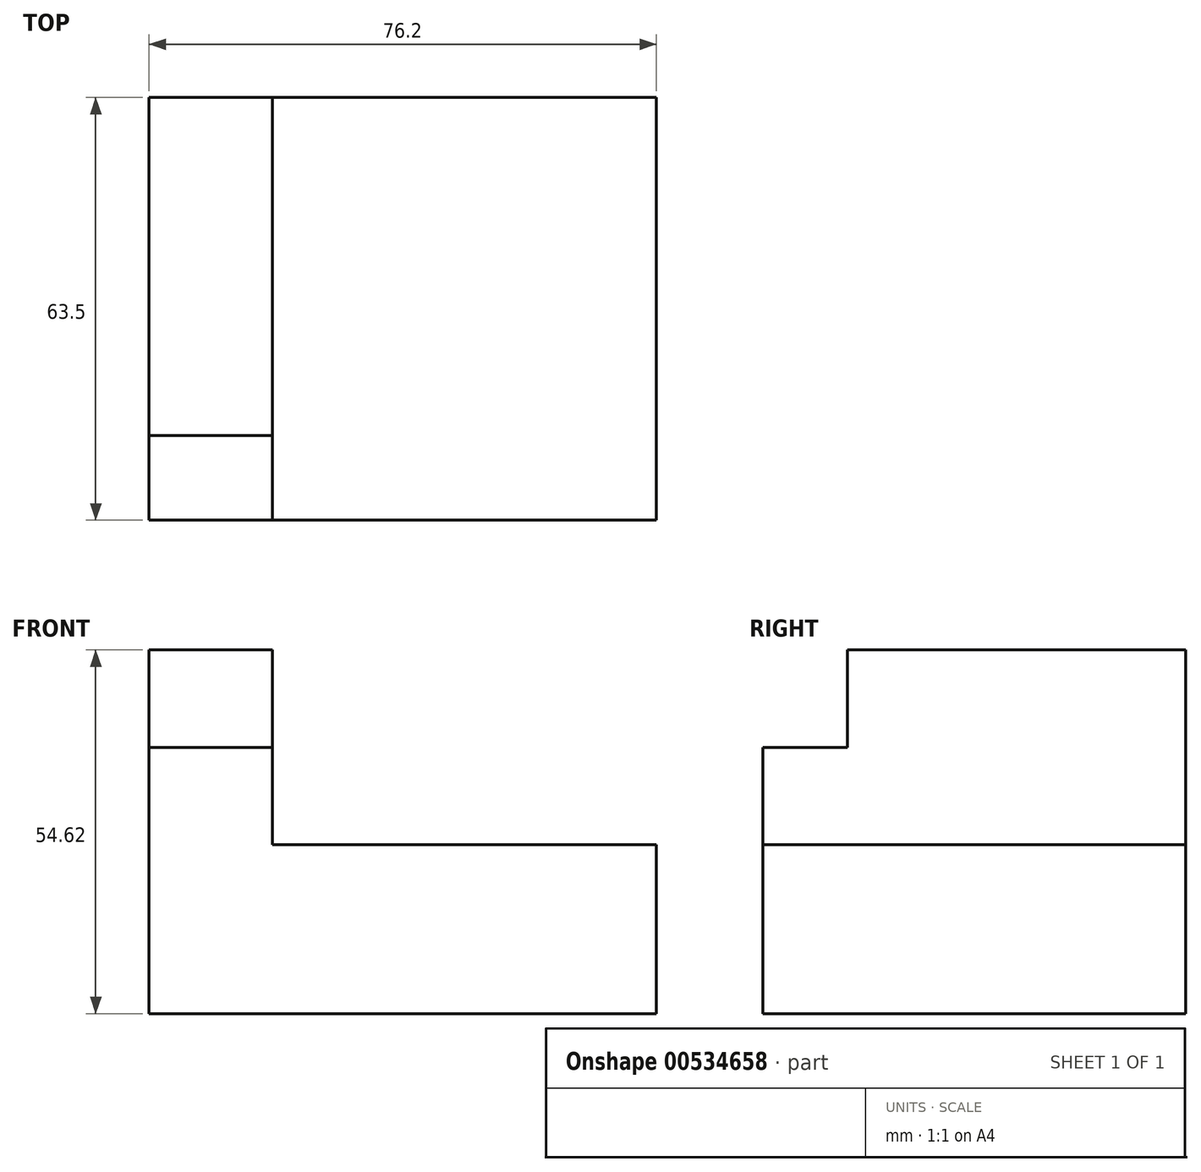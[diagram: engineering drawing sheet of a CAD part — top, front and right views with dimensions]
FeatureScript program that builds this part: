
annotation { "Feature Type Name" : "Feature", "Feature Type Description" : "" }
export const myFeature = defineFeature(function(context is Context, id is Id, definition is map)
    precondition{}
    {
        {
            var Q0;
            Q0=qCreatedBy(makeId("Top.planeOp"),FACE);
            var sketch = newSketch(context, id + "F0", { "sketchPlane" : qUnion([Q0])});
            skLineSegment(sketch, "E0.bottom", {"start": v(-36.12, 34.38) * mm, "end": v(40.08, 34.38) * mm});
            skLineSegment(sketch, "E0.top", {"start": v(-36.12, -29.12) * mm, "end": v(40.08, -29.12) * mm});
            skLineSegment(sketch, "E0.left", {"start": v(-36.12, 34.38) * mm, "end": v(-36.12, -29.12) * mm});
            skLineSegment(sketch, "E0.right", {"start": v(40.08, 34.38) * mm, "end": v(40.08, -29.12) * mm});
            skSolve(sketch);
        }
        {
            var Q0;
            Q0=makeQuery(id+"F0.imprint","IMPRINT",FACE,{"disambiguationData":[TD([[makeQuery(id+"F0.imprint","IMPRINT",EDGE,{"derivedFrom":sQuery(id+"F0.wireOp",EDGE,"E0.bottom")}),-1.0]])]});
            extrude(context, id + "F1", {"entities" : qUnion([Q0]), "depth" : 25.4 * mm, "offsetDistance" : 25.4 * mm});
        }
        {
            var Q0;
            Q0=makeQuery(id+"F1.opExtrude","SWEPT_FACE",FACE,{"disambiguationData":[OSD([sQuery(id+"F0.wireOp",EDGE,"E0.top")])]});
            var sketch = newSketch(context, id + "F2", { "sketchPlane" : qUnion([Q0])});
            skLineSegment(sketch, "E1.bottom", {"start": v(-36.12, 25.4) * mm, "end": v(-17.59, 25.4) * mm});
            skLineSegment(sketch, "E1.top", {"start": v(-36.12, 54.62) * mm, "end": v(-17.59, 54.62) * mm});
            skLineSegment(sketch, "E1.left", {"start": v(-36.12, 25.4) * mm, "end": v(-36.12, 54.62) * mm});
            skLineSegment(sketch, "E1.right", {"start": v(-17.59, 25.4) * mm, "end": v(-17.59, 54.62) * mm});
            skSolve(sketch);
        }
        {
            var Q0;
            Q0=makeQuery(id+"F2.imprint","IMPRINT",FACE,{"disambiguationData":[TD([[makeQuery(id+"F2.imprint","IMPRINT",EDGE,{"derivedFrom":sQuery(id+"F2.wireOp",EDGE,"E1.bottom")}),1.0]])]});
            extrude(context, id + "F3", {"entities" : qUnion([Q0]), "operationType" : NewBodyOperationType.ADD, "oppositeDirection" : true, "depth" : 63.5 * mm, "offsetDistance" : 25.4 * mm});
        }
        {
            var Q0;
            Q0=makeQuery(id+"F3.boolean.opBoolean","MERGE",FACE,{"derivedFrom":[makeQuery(id+"F1.opExtrude","SWEPT_FACE",FACE,{"disambiguationData":[OSD([sQuery(id+"F0.wireOp",EDGE,"E0.top")])]}),makeQuery(id+"F3.opExtrude","CAP_FACE",FACE,{"disambiguationData":[OSD([sQuery(id+"F2.wireOp",EDGE,"E1.bottom"),sQuery(id+"F2.wireOp",EDGE,"E1.top"),sQuery(id+"F2.wireOp",EDGE,"E1.left"),sQuery(id+"F2.wireOp",EDGE,"E1.right")])],"isStart":true})]});
            var sketch = newSketch(context, id + "F4", { "sketchPlane" : qUnion([Q0])});
            skLineSegment(sketch, "E2.bottom", {"start": v(-36.12, 56.15) * mm, "end": v(-17.59, 56.15) * mm});
            skLineSegment(sketch, "E2.top", {"start": v(-36.12, 40.01) * mm, "end": v(-17.59, 40.01) * mm});
            skLineSegment(sketch, "E2.left", {"start": v(-36.12, 56.15) * mm, "end": v(-36.12, 40.01) * mm});
            skLineSegment(sketch, "E2.right", {"start": v(-17.59, 56.15) * mm, "end": v(-17.59, 40.01) * mm});
            skSolve(sketch);
        }
        {
            var Q0;
            {var subQ0=sQuery(id+"F4.wireOp",EDGE,"E2.top");Q0=makeQuery(id+"F4.imprint","IMPRINT",FACE,{"disambiguationData":[TD([[makeQuery(id+"F4.imprint","IMPRINT",EDGE,{"derivedFrom":subQ0}),1.0]])]});}
            extrude(context, id + "F5", {"entities" : qUnion([Q0]), "operationType" : NewBodyOperationType.REMOVE, "oppositeDirection" : true, "depth" : 12.7 * mm, "offsetDistance" : 25.4 * mm});
        }
    });
